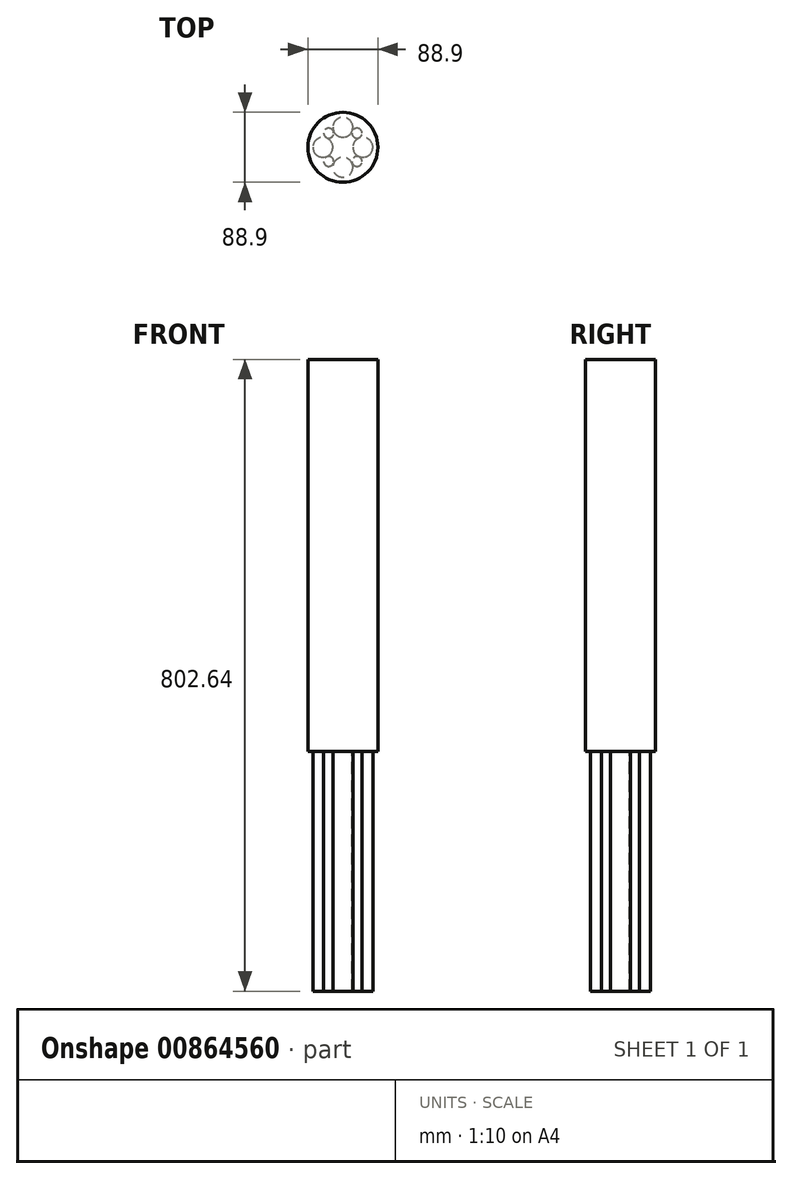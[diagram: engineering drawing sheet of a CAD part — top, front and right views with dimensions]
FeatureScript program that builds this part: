
annotation { "Feature Type Name" : "Feature", "Feature Type Description" : "" }
export const myFeature = defineFeature(function(context is Context, id is Id, definition is map)
    precondition{}
    {
        {
            var Q0;
            Q0=qCreatedBy(makeId("Top.planeOp"),FACE);
            var sketch = newSketch(context, id + "F0", { "sketchPlane" : qUnion([Q0])});
            skCircle(sketch, "E0", {"center": v(0, 0) * mm, "radius": 44.45 * mm});
            skSolve(sketch);
        }
        {
            var Q0;
            Q0=makeQuery(id+"F0.imprint","IMPRINT",FACE,{"disambiguationData":[TD([[makeQuery(id+"F0.imprint","IMPRINT",EDGE,{"derivedFrom":sQuery(id+"F0.wireOp",EDGE,"E0")}),1.0]])]});
            extrude(context, id + "F1", {"entities" : qUnion([Q0]), "oppositeDirection" : true, "depth" : 497.84 * mm, "offsetDistance" : 25.4 * mm});
        }
        {
            var Q0;
            Q0=makeQuery(id+"F1.opExtrude","CAP_FACE",FACE,{"disambiguationData":[OSD([sQuery(id+"F0.wireOp",EDGE,"E0")])],"isStart":false});
            var sketch = newSketch(context, id + "F2", { "sketchPlane" : qUnion([Q0])});
            skCircle(sketch, "E1", {"center": v(0, 0) * mm, "radius": 25.4 * mm, "construction": true});
            skLineSegment(sketch, "E2", {"start": v(0, 0) * mm, "end": v(0, 25.4) * mm, "construction": true});
            skLineSegment(sketch, "E3", {"start": v(0, 0) * mm, "end": v(0, -25.4) * mm, "construction": true});
            skLineSegment(sketch, "E4", {"start": v(-25.4, 0) * mm, "end": v(25.4, 0) * mm, "construction": true});
            skLineSegment(sketch, "E5", {"start": v(-17.96, -17.96) * mm, "end": v(17.96, 17.96) * mm, "construction": true});
            skLineSegment(sketch, "E6", {"start": v(-17.96, 17.96) * mm, "end": v(17.96, -17.96) * mm, "construction": true});
            skCircle(sketch, "E7", {"center": v(0, 25.4) * mm, "radius": 12.7 * mm});
            skCircle(sketch, "E8", {"center": v(0, -25.4) * mm, "radius": 12.7 * mm});
            skCircle(sketch, "E9", {"center": v(-25.4, 0) * mm, "radius": 12.7 * mm});
            skCircle(sketch, "E10", {"center": v(25.4, 0) * mm, "radius": 12.7 * mm});
            skCircle(sketch, "E11", {"center": v(-17.96, 17.96) * mm, "radius": 6.35 * mm});
            skCircle(sketch, "E12", {"center": v(17.96, 17.96) * mm, "radius": 6.35 * mm});
            skCircle(sketch, "E13", {"center": v(17.96, -17.96) * mm, "radius": 6.35 * mm});
            skCircle(sketch, "E14", {"center": v(-17.96, -17.96) * mm, "radius": 6.35 * mm});
            skSolve(sketch);
        }
        {
            var Q0;
            Q0 = qSketchRegion(id + "F2", true);
            extrude(context, id + "F3", {"entities" : qUnion([Q0]), "operationType" : NewBodyOperationType.ADD, "depth" : 304.8 * mm, "offsetDistance" : 25.4 * mm});
        }
    });
